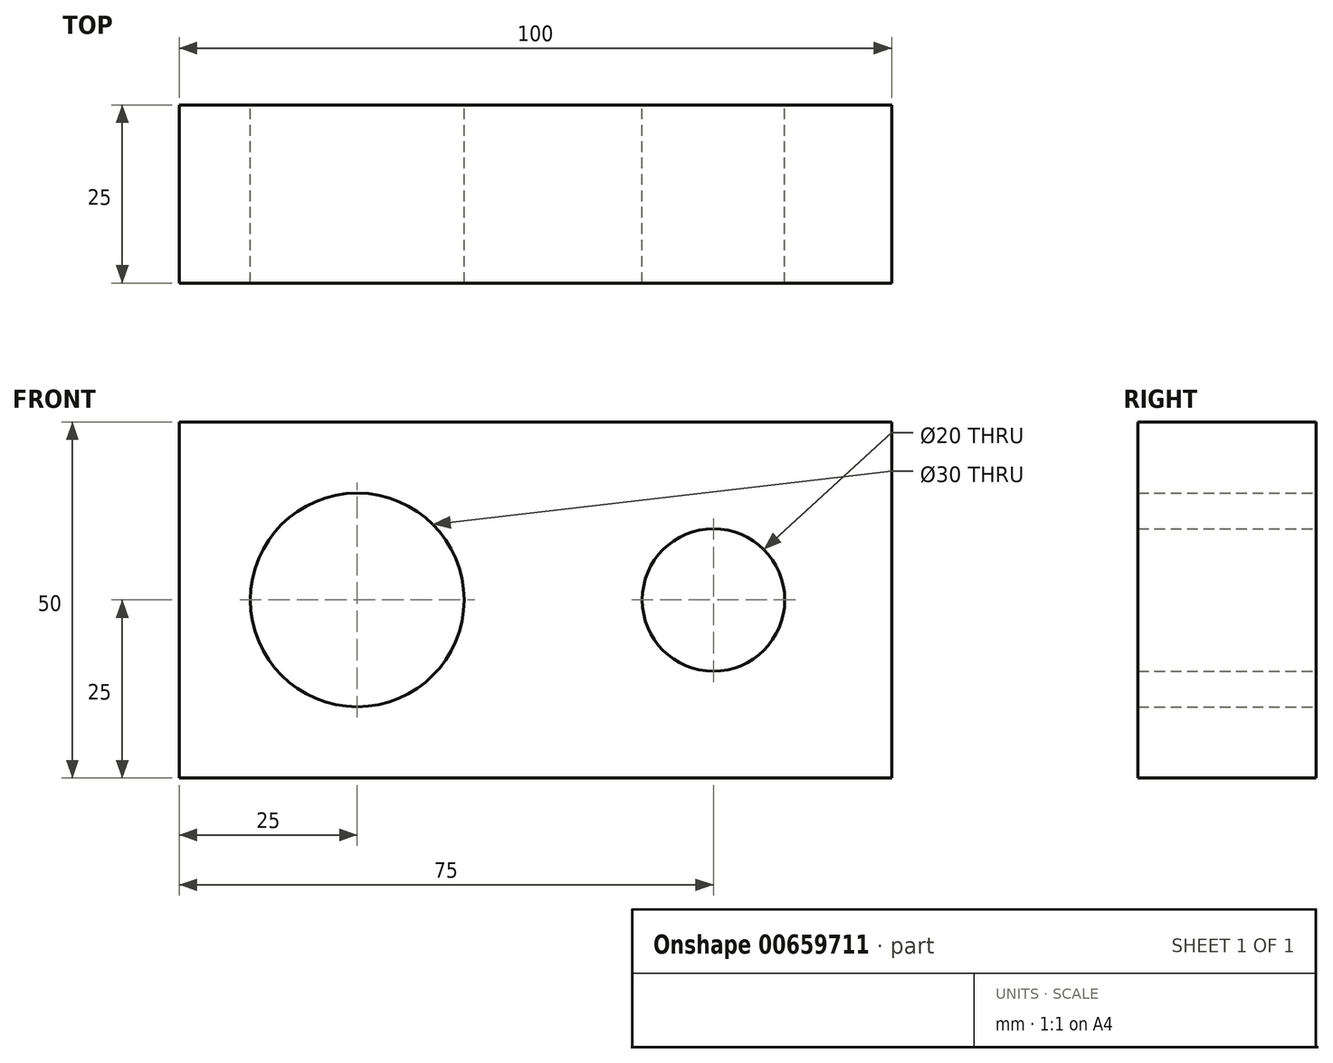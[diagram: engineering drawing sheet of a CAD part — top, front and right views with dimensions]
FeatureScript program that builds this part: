
annotation { "Feature Type Name" : "Feature", "Feature Type Description" : "" }
export const myFeature = defineFeature(function(context is Context, id is Id, definition is map)
    precondition{}
    {
        {
            var Q0;
            Q0=qCreatedBy(makeId("Front.planeOp"),FACE);
            var sketch = newSketch(context, id + "F0", { "sketchPlane" : qUnion([Q0])});
            skLineSegment(sketch, "E0.bottom", {"start": v(-50, -25) * mm, "end": v(50, -25) * mm});
            skLineSegment(sketch, "E0.top", {"start": v(-50, 25) * mm, "end": v(50, 25) * mm});
            skLineSegment(sketch, "E0.left", {"start": v(-50, -25) * mm, "end": v(-50, 25) * mm});
            skLineSegment(sketch, "E0.right", {"start": v(50, -25) * mm, "end": v(50, 25) * mm});
            skPoint(sketch, "E0.middle", {"position": v(0, 0) * mm});
            skCircle(sketch, "E1", {"center": v(25, 0) * mm, "radius": 10 * mm});
            skCircle(sketch, "E2", {"center": v(-25, 0) * mm, "radius": 15 * mm});
            skSolve(sketch);
        }
        {
            var Q0;
            Q0=makeQuery(id+"F0.imprint","IMPRINT",FACE,{"disambiguationData":[TD([[makeQuery(id+"F0.imprint","IMPRINT",EDGE,{"derivedFrom":sQuery(id+"F0.wireOp",EDGE,"E0.bottom")}),1.0]])]});
            extrude(context, id + "F1", {"entities" : qUnion([Q0]), "depth" : 25 * mm, "offsetDistance" : 25 * mm});
        }
    });
